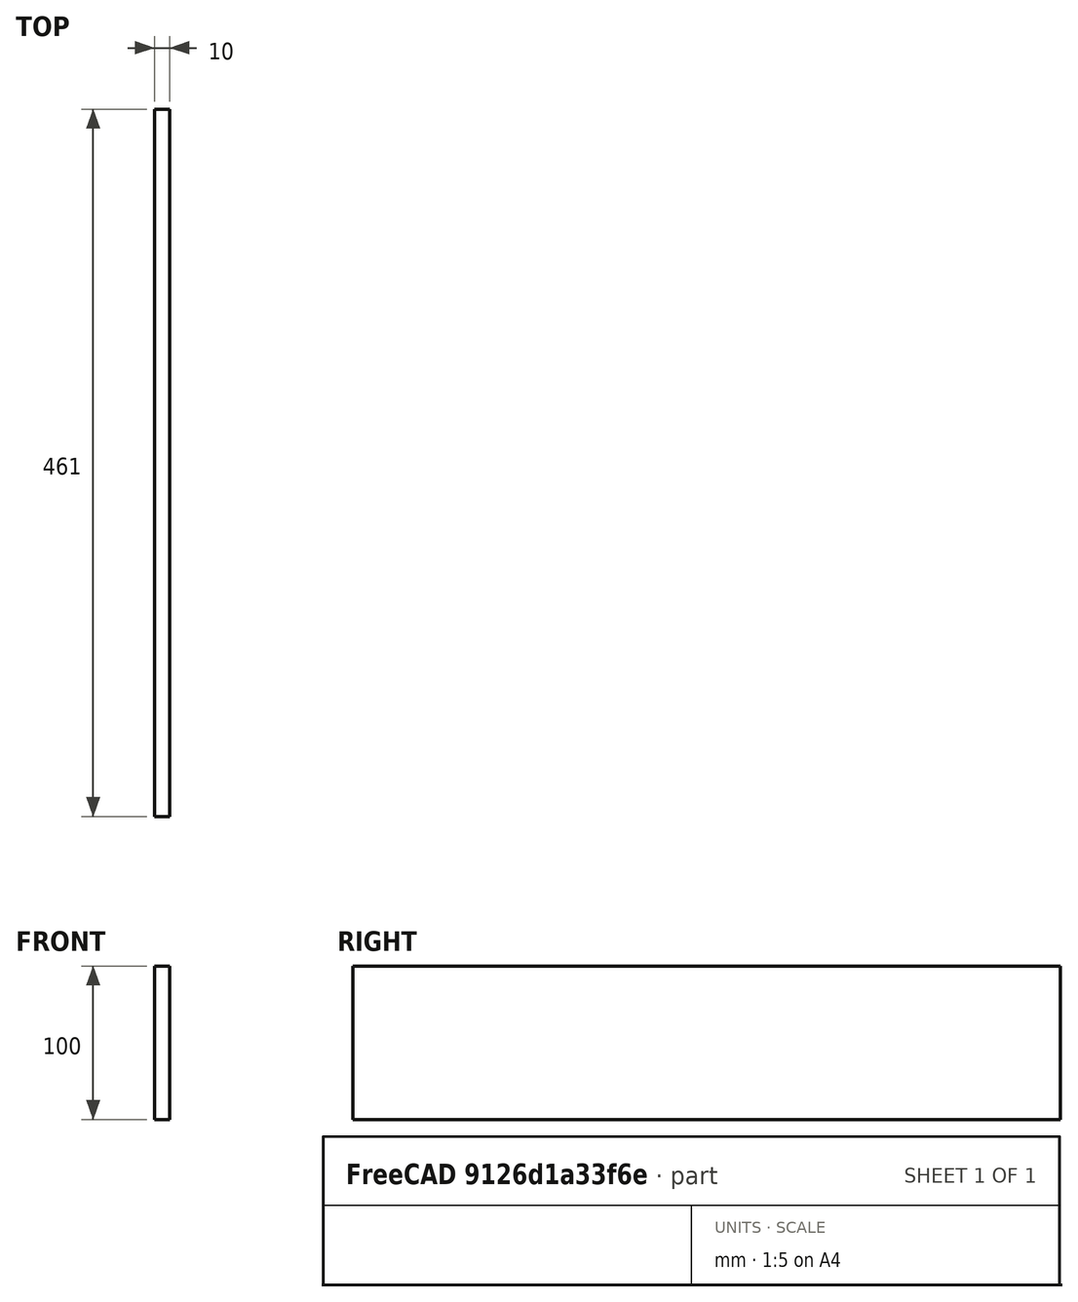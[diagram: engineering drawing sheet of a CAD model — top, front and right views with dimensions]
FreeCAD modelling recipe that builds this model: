
FCSTD DOCUMENT  (FreeCAD 0.18R16131 (Git))
Label: 500_Front_YZ_3
License: All rights reserved
LicenseURL: http://en.wikipedia.org/wiki/All_rights_reserved
objects: Sketcher::SketchObject×1, Spreadsheet::Sheet×1, PartDesign::Pad×1, PartDesign::Body×1
note: 4 computed .brp shape members not serialized (recipe doc carries the construction recipe); baked Part::Feature solids carry a one-line shape summary decoded from their .brp

FEATURE [Sketcher::SketchObject] Sketch
  MapMode = 4
  Placement = pos=(0,0,0) rot=(0.57735,0.57735,0.57735;2.0944rad)
  Support = -> [XY_Plane]
  expr: Constraints[6] = Spreadsheet.nY
  expr: Constraints[5] = Spreadsheet.nZ
  sketch-geometry (5):
    g0: LineSegment StartX=0 StartY=0 StartZ=0 EndX=0 EndY=100 EndZ=0
    g1: LineSegment StartX=461 StartY=0 StartZ=0 EndX=461 EndY=100 EndZ=0
    g2: LineSegment StartX=461 StartY=100 StartZ=0 EndX=0 EndY=100 EndZ=0
    g3: LineSegment StartX=230.5 StartY=0 StartZ=0 EndX=0 EndY=0 EndZ=0
    g4: LineSegment StartX=461 StartY=0 StartZ=0 EndX=230.5 EndY=0 EndZ=0
  constraints (14):
    c: Vertical(g0)
    c: Vertical(g1)
    c: Coincident(g2,g1)
    c: Coincident(g2,g0)
    c: Horizontal(g2)
    c: DistanceY(g1,g1) = 100
    c: DistanceX(g2,g2) = 461
    c: Coincident(g3,g0)
    c: Coincident(g4,g1)
    c: Horizontal(g4)
    c: Equal(g3,g4)
    c: Coincident(g4,g3)
    c: Horizontal(g3)
    c: Coincident(g0,g-1)
FEATURE [Spreadsheet::Sheet] Spreadsheet  label="xls"
  cells = B7=KEYBOARD FRONT; B8=Width; C8=nY; D8(nY)==480 - 19; B9=Height; C9=nZ; D9(nZ)=100; E9=F(T); B10=Thickness; C10=nT; D10(nT)=10
FEATURE [PartDesign::Pad] Pad
  Length = 10
  Length2 = 100
  Profile = -> Sketch
  Reversed = true
  Type = 0
  expr: Length = Spreadsheet.nT
FEATURE [PartDesign::Body] Body
  Group = -> [Sketch,Pad]
  Origin = -> Origin
  Tip = -> Pad
